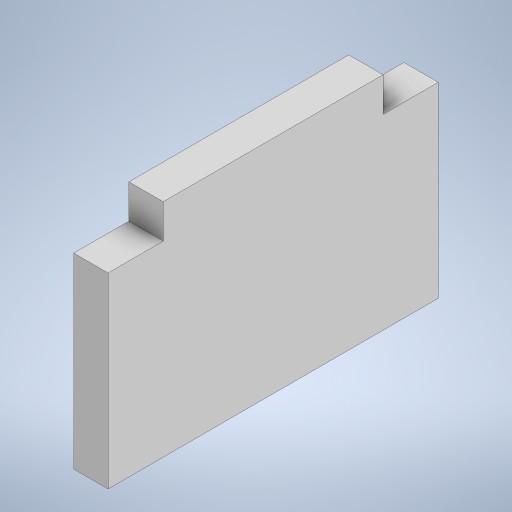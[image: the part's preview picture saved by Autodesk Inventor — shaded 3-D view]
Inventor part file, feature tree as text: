
AUTODESK INVENTOR PART (.ipt)
format: ipt  version: 2024 (Build 280153000, 153)  size: 210,432 bytes
history: native  units: mm
features: extrude x2, sketch x2
ambient origin geometry x8: Origin, YZ Plane, XZ Plane, XY Plane, X Axis, Y Axis, Z Axis, Center Point
bodies: Solid1 (feature_tree)
feature tree (4):
  extrude  "Extrusion1"  Depth=30.0mm
  extrude  "Extrusion2"  Depth=3.125mm
  sketch  "Sketch1"  dims[d0=3.125mm d1=30.0mm]
  sketch  "Sketch3"  dims[d2=17.0mm d3=0.0mm d4=3.125mm d5=19.98mm d6=3.1mm d7=0.0mm]
